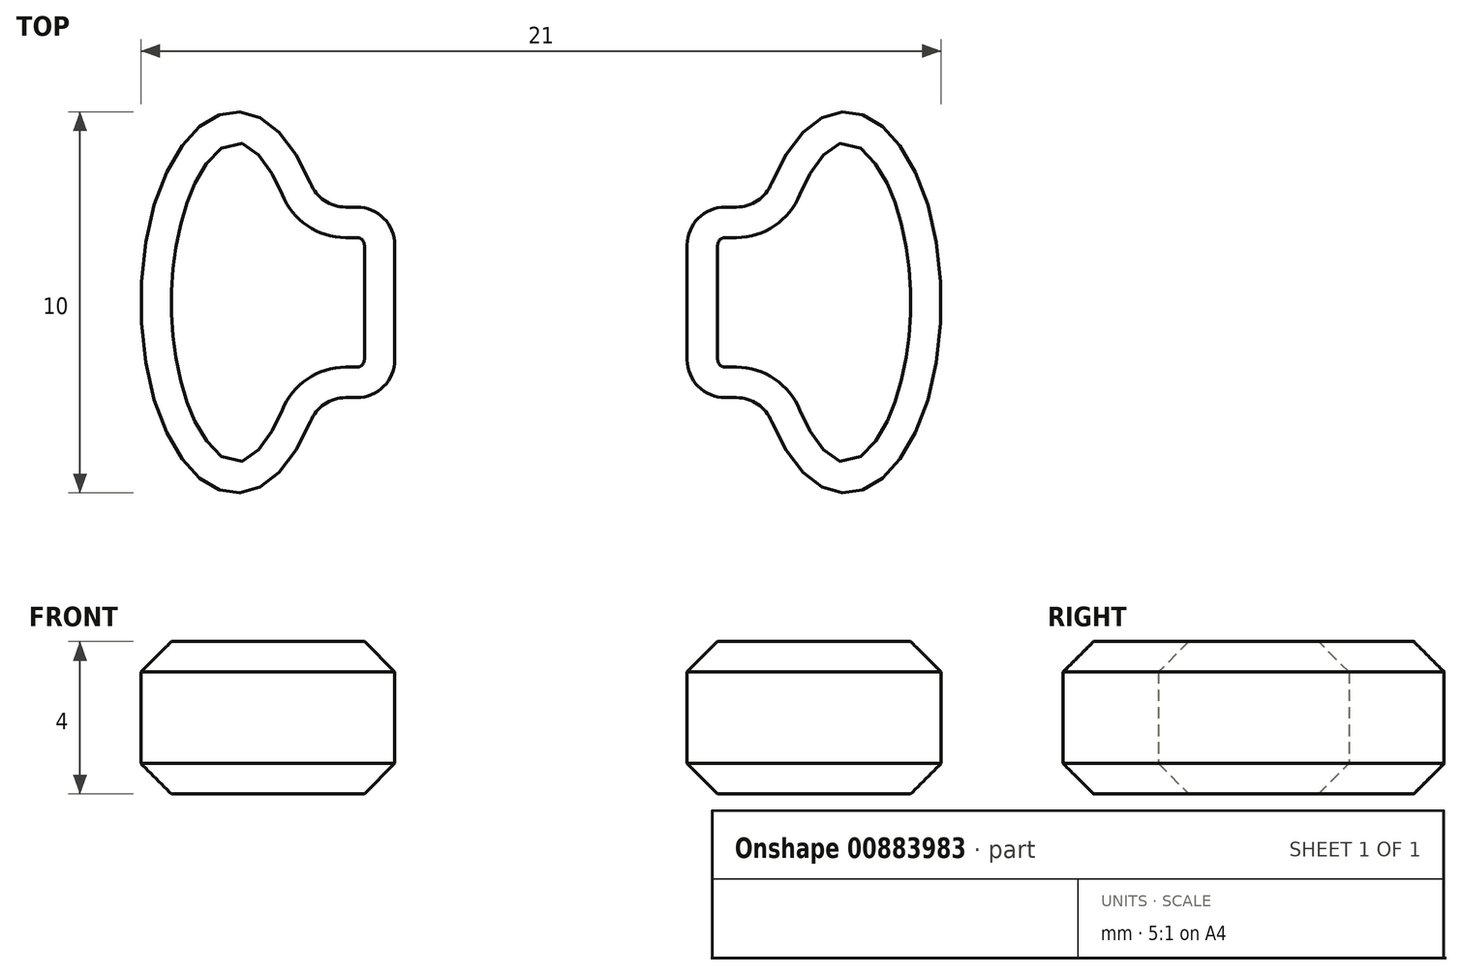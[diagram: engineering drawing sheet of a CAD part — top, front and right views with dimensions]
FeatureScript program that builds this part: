
annotation { "Feature Type Name" : "Feature", "Feature Type Description" : "" }
export const myFeature = defineFeature(function(context is Context, id is Id, definition is map)
    precondition{}
    {
        {
            var Q0;
            Q0=qCreatedBy(makeId("Top.planeOp"),FACE);
            var sketch = newSketch(context, id + "F0", { "sketchPlane" : qUnion([Q0])});
            skEllipticalArc(sketch, "E0", {});
            skFitSpline(sketch, "E1.0", {"points": [v(-8.64, -6.96) * mm, v(-8, -7.02) * mm, v(-7.36, -6.96) * mm, v(-6.76, -6.78) * mm, v(-6.23, -6.5) * mm, v(-5.6, -6.06) * mm, v(-4.98, -5.37) * mm, v(-4.42, -4.45) * mm, v(-4, -3.43) * mm, v(-3.71, -2.32) * mm, v(-3.54, -1.18) * mm, v(-3.48, 0) * mm, v(-3.54, 1.18) * mm, v(-3.71, 2.32) * mm, v(-4, 3.43) * mm, v(-4.42, 4.45) * mm, v(-4.98, 5.37) * mm, v(-5.6, 6.06) * mm, v(-6.23, 6.5) * mm, v(-6.76, 6.78) * mm, v(-7.36, 6.96) * mm, v(-8, 7.02) * mm, v(-8.64, 6.96) * mm, v(-9.24, 6.78) * mm, v(-9.77, 6.5) * mm, v(-10.4, 6.06) * mm, v(-11.02, 5.37) * mm, v(-11.58, 4.45) * mm, v(-12, 3.43) * mm, v(-12.29, 2.32) * mm, v(-12.46, 1.18) * mm, v(-12.52, 0) * mm, v(-12.46, -1.18) * mm, v(-12.29, -2.32) * mm, v(-12, -3.43) * mm, v(-11.58, -4.45) * mm, v(-11.02, -5.37) * mm, v(-10.4, -6.06) * mm, v(-9.77, -6.5) * mm, v(-9.24, -6.78) * mm, v(-8.64, -6.96) * mm, v(-8, -7.02) * mm, v(-7.36, -6.96) * mm]});
            skLineSegment(sketch, "E2", {"start": v(-2.55, -5.67) * mm, "end": v(-7.16, -6.9) * mm});
            skLineSegment(sketch, "E3", {"start": v(-2.55, 5.67) * mm, "end": v(-7.16, 6.9) * mm});
            skLineSegment(sketch, "E4", {"start": v(-5.12, 2.5) * mm, "end": v(-4.83, 2.5) * mm});
            skLineSegment(sketch, "E5", {"start": v(-3.83, 1.5) * mm, "end": v(-3.83, -1.5) * mm});
            skLineSegment(sketch, "E6", {"start": v(-4.83, -2.5) * mm, "end": v(-5.12, -2.5) * mm});
            skPoint(sketch, "E7.visualSharp", {"position": v(-5.83, 2.5) * mm});
            skArc(sketch, "E7.filletArc", {"start": v(-6.05, 3.13) * mm, "mid": v(-5.68, 2.67) * mm, "end": v(-5.12, 2.5) * mm});
            skPoint(sketch, "E8.visualSharp", {"position": v(-5.83, -2.5) * mm});
            skArc(sketch, "E8.filletArc", {"start": v(-5.12, -2.5) * mm, "mid": v(-5.68, -2.67) * mm, "end": v(-6.05, -3.13) * mm});
            skPoint(sketch, "E9.visualSharp", {"position": v(-3.83, 2.5) * mm});
            skArc(sketch, "E9.filletArc", {"start": v(-3.83, 1.5) * mm, "mid": v(-4.13, 2.2) * mm, "end": v(-4.83, 2.5) * mm});
            skPoint(sketch, "E10.visualSharp", {"position": v(-3.83, -2.5) * mm});
            skArc(sketch, "E10.filletArc", {"start": v(-4.83, -2.5) * mm, "mid": v(-4.13, -2.2) * mm, "end": v(-3.83, -1.5) * mm});
            skEllipticalArc(sketch, "E11", {});
            skLineSegment(sketch, "E12", {"start": v(5.12, 2.5) * mm, "end": v(4.83, 2.5) * mm});
            skLineSegment(sketch, "E13", {"start": v(3.83, 1.5) * mm, "end": v(3.83, -1.5) * mm});
            skLineSegment(sketch, "E14", {"start": v(4.83, -2.5) * mm, "end": v(5.12, -2.5) * mm});
            skFitSpline(sketch, "E15.0", {"points": [v(8.64, 6.96) * mm, v(8, 7.02) * mm, v(7.36, 6.96) * mm, v(6.76, 6.78) * mm, v(6.23, 6.5) * mm, v(5.6, 6.06) * mm, v(4.98, 5.37) * mm, v(4.42, 4.45) * mm, v(4, 3.43) * mm, v(3.71, 2.32) * mm, v(3.54, 1.18) * mm, v(3.48, 0) * mm, v(3.54, -1.18) * mm, v(3.71, -2.32) * mm, v(4, -3.43) * mm, v(4.42, -4.45) * mm, v(4.98, -5.37) * mm, v(5.6, -6.06) * mm, v(6.23, -6.5) * mm, v(6.76, -6.78) * mm, v(7.36, -6.96) * mm, v(8, -7.02) * mm, v(8.64, -6.96) * mm, v(9.24, -6.78) * mm, v(9.77, -6.5) * mm, v(10.4, -6.06) * mm, v(11.02, -5.37) * mm, v(11.58, -4.45) * mm, v(12, -3.43) * mm, v(12.29, -2.32) * mm, v(12.46, -1.18) * mm, v(12.52, 0) * mm, v(12.46, 1.18) * mm, v(12.29, 2.32) * mm, v(12, 3.43) * mm, v(11.58, 4.45) * mm, v(11.02, 5.37) * mm, v(10.4, 6.06) * mm, v(9.77, 6.5) * mm, v(9.24, 6.78) * mm, v(8.64, 6.96) * mm, v(8, 7.02) * mm, v(7.36, 6.96) * mm]});
            skLineSegment(sketch, "E16", {"start": v(2.55, 5.67) * mm, "end": v(7.16, 6.9) * mm});
            skLineSegment(sketch, "E17", {"start": v(2.55, -5.67) * mm, "end": v(7.16, -6.9) * mm});
            skPoint(sketch, "E18.visualSharp", {"position": v(3.83, 2.5) * mm});
            skArc(sketch, "E18.filletArc", {"start": v(4.83, 2.5) * mm, "mid": v(4.13, 2.2) * mm, "end": v(3.83, 1.5) * mm});
            skPoint(sketch, "E19.visualSharp", {"position": v(3.83, -2.5) * mm});
            skArc(sketch, "E19.filletArc", {"start": v(3.83, -1.5) * mm, "mid": v(4.13, -2.2) * mm, "end": v(4.83, -2.5) * mm});
            skPoint(sketch, "E20.visualSharp", {"position": v(5.83, -2.5) * mm});
            skArc(sketch, "E20.filletArc", {"start": v(6.05, -3.13) * mm, "mid": v(5.68, -2.67) * mm, "end": v(5.12, -2.5) * mm});
            skPoint(sketch, "E21.visualSharp", {"position": v(5.83, 2.5) * mm});
            skArc(sketch, "E21.filletArc", {"start": v(5.12, 2.5) * mm, "mid": v(5.68, 2.67) * mm, "end": v(6.05, 3.13) * mm});
            skPoint(sketch, "E22.visualSharp", {"position": v(0, 5) * mm});
            skArc(sketch, "E22.filletArc", {"start": v(-2.55, 5.67) * mm, "mid": v(0, 5.34) * mm, "end": v(2.55, 5.67) * mm});
            skPoint(sketch, "E23.visualSharp", {"position": v(0, -5) * mm});
            skArc(sketch, "E23.filletArc", {"start": v(2.55, -5.67) * mm, "mid": v(0, -5.34) * mm, "end": v(-2.55, -5.67) * mm});
            const initialGuessF0  = {"E0": [-0.008, 0, 0, -1, 0.005, 0.0025, 2.2466633627272605, 0.8949292908625334], "E11": [0.008, 0, 0, 1, 0.005, 0.0025, 2.2466633627272605, 0.8949292908625334]};
            skSetInitialGuess(sketch, initialGuessF0);
            skSolve(sketch);
        }
        {
            var Q0;
            Q0=qSketchRegion(id+"F0",true);
            extrude(context, id + "F1", {"entities" : qUnion([Q0]), "depth" : 4 * mm, "offsetDistance" : 25 * mm});
        }
        {
            var Q0;
            Q0=makeQuery(id+"F1.opExtrude","CAP_FACE",FACE,{"disambiguationData":[OSD([sQuery(id+"F0.wireOp",EDGE,"E0"),sQuery(id+"F0.wireOp",EDGE,"E1.0"),sQuery(id+"F0.wireOp",EDGE,"E2"),sQuery(id+"F0.wireOp",EDGE,"E3"),sQuery(id+"F0.wireOp",EDGE,"E4"),sQuery(id+"F0.wireOp",EDGE,"E5"),sQuery(id+"F0.wireOp",EDGE,"E6"),sQuery(id+"F0.wireOp",EDGE,"E7.filletArc"),sQuery(id+"F0.wireOp",EDGE,"E8.filletArc"),sQuery(id+"F0.wireOp",EDGE,"E9.filletArc"),sQuery(id+"F0.wireOp",EDGE,"E10.filletArc"),sQuery(id+"F0.wireOp",EDGE,"E11"),sQuery(id+"F0.wireOp",EDGE,"E12"),sQuery(id+"F0.wireOp",EDGE,"E13"),sQuery(id+"F0.wireOp",EDGE,"E14"),sQuery(id+"F0.wireOp",EDGE,"E15.0"),sQuery(id+"F0.wireOp",EDGE,"E16"),sQuery(id+"F0.wireOp",EDGE,"E17"),sQuery(id+"F0.wireOp",EDGE,"E18.filletArc"),sQuery(id+"F0.wireOp",EDGE,"E19.filletArc"),sQuery(id+"F0.wireOp",EDGE,"E20.filletArc"),sQuery(id+"F0.wireOp",EDGE,"E21.filletArc"),sQuery(id+"F0.wireOp",EDGE,"E22.filletArc"),sQuery(id+"F0.wireOp",EDGE,"E23.filletArc")])],"isStart":false});
            var Q1;
            Q1=makeQuery(id+"F1.opExtrude","CAP_FACE",FACE,{"disambiguationData":[OSD([sQuery(id+"F0.wireOp",EDGE,"E0"),sQuery(id+"F0.wireOp",EDGE,"E1.0"),sQuery(id+"F0.wireOp",EDGE,"E2"),sQuery(id+"F0.wireOp",EDGE,"E3"),sQuery(id+"F0.wireOp",EDGE,"E4"),sQuery(id+"F0.wireOp",EDGE,"E5"),sQuery(id+"F0.wireOp",EDGE,"E6"),sQuery(id+"F0.wireOp",EDGE,"E7.filletArc"),sQuery(id+"F0.wireOp",EDGE,"E8.filletArc"),sQuery(id+"F0.wireOp",EDGE,"E9.filletArc"),sQuery(id+"F0.wireOp",EDGE,"E10.filletArc"),sQuery(id+"F0.wireOp",EDGE,"E11"),sQuery(id+"F0.wireOp",EDGE,"E12"),sQuery(id+"F0.wireOp",EDGE,"E13"),sQuery(id+"F0.wireOp",EDGE,"E14"),sQuery(id+"F0.wireOp",EDGE,"E15.0"),sQuery(id+"F0.wireOp",EDGE,"E16"),sQuery(id+"F0.wireOp",EDGE,"E17"),sQuery(id+"F0.wireOp",EDGE,"E18.filletArc"),sQuery(id+"F0.wireOp",EDGE,"E19.filletArc"),sQuery(id+"F0.wireOp",EDGE,"E20.filletArc"),sQuery(id+"F0.wireOp",EDGE,"E21.filletArc"),sQuery(id+"F0.wireOp",EDGE,"E22.filletArc"),sQuery(id+"F0.wireOp",EDGE,"E23.filletArc")])],"isStart":true});
            chamfer(context, id + "F2", {"entities" : qUnion([Q0, Q1]), "width" : .8 * mm, "tangentPropagation" : true});
        }
    });
